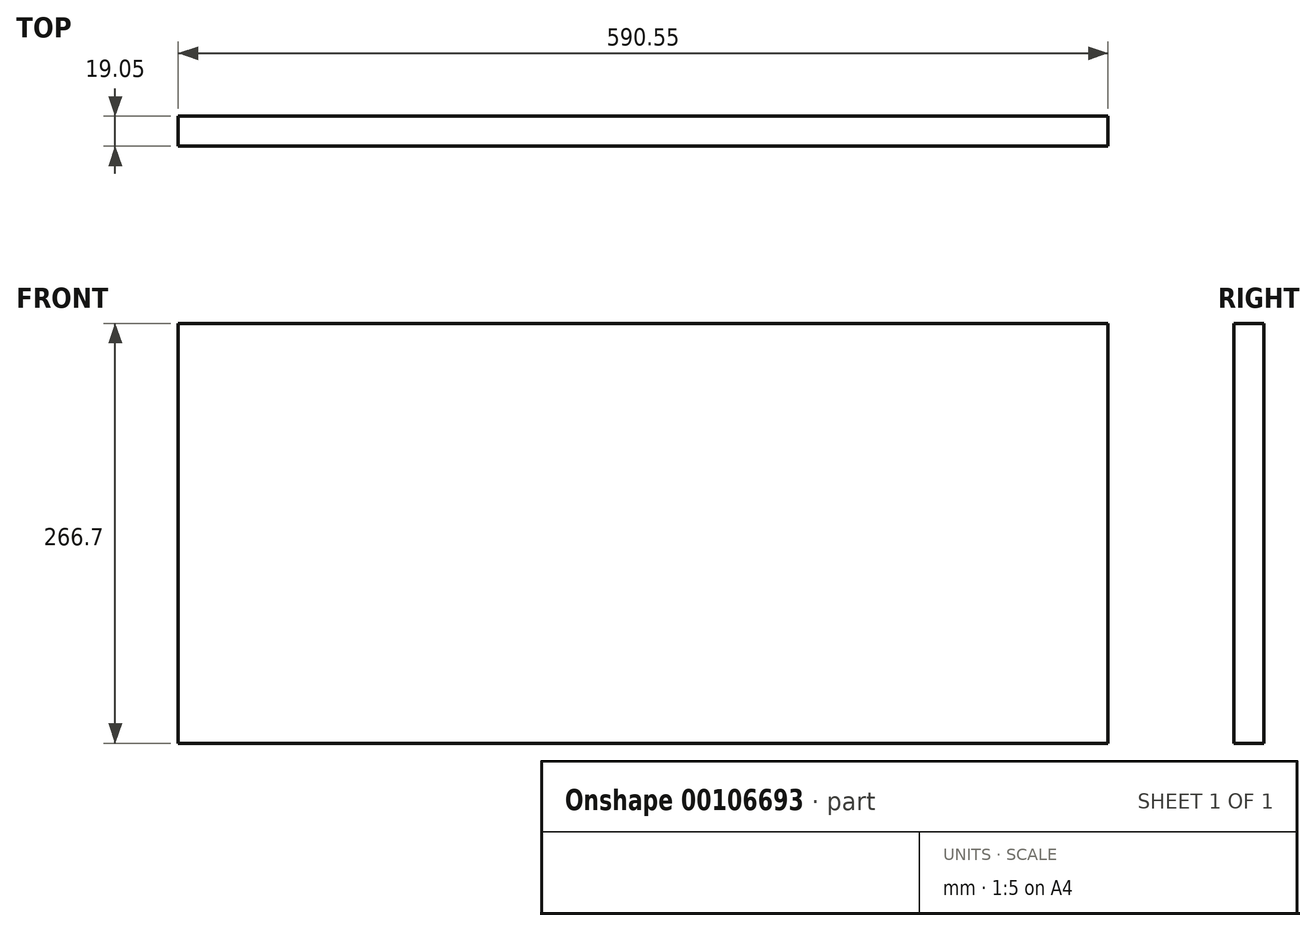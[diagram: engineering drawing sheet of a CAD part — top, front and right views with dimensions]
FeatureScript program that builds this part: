
annotation { "Feature Type Name" : "Feature", "Feature Type Description" : "" }
export const myFeature = defineFeature(function(context is Context, id is Id, definition is map)
    precondition{}
    {
        {
            var Q0;
            Q0=qCreatedBy(makeId("Front.planeOp"),FACE);
            var sketch = newSketch(context, id + "F0", { "sketchPlane" : qUnion([Q0])});
            skLineSegment(sketch, "E0.bottom", {"start": v(0, 0) * mm, "end": v(590.55, 0) * mm});
            skLineSegment(sketch, "E0.top", {"start": v(0, 266.7) * mm, "end": v(590.55, 266.7) * mm});
            skLineSegment(sketch, "E0.left", {"start": v(0, 0) * mm, "end": v(0, 266.7) * mm});
            skLineSegment(sketch, "E0.right", {"start": v(590.55, 0) * mm, "end": v(590.55, 266.7) * mm});
            skSolve(sketch);
        }
        {
            var Q0;
            Q0=makeQuery(id+"F0.imprint","IMPRINT",FACE,{"disambiguationData":[TD([[makeQuery(id+"F0.imprint","IMPRINT",EDGE,{"derivedFrom":sQuery(id+"F0.wireOp",EDGE,"E0.bottom")}),1.0]])]});
            extrude(context, id + "F1", {"entities" : qUnion([Q0]), "depth" : 19.05 * mm});
        }
    });
